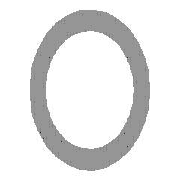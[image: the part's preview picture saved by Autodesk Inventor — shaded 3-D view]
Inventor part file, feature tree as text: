
AUTODESK INVENTOR PART (.ipt)
format: ipt  version: 2021 (Build 250183000, 183)  size: 224,768 bytes
history: native  units: mm (DEFAULTED — no unit token found)
features: other x5, plane x2, sketch x2, sweep x1
ambient origin geometry x8: Origin, YZ Plane, XZ Plane, XY Plane, X Axis, Y Axis, Z Axis, Center Point
bodies: Solid1 (feature_tree)
feature tree (10):
  parser-record x1  (decoder bookkeeping rows leaked as tree rows — omitted from the tree; the rows remain in map.json)
  other  "Driven Length"
  other  "Plano inicial"
  other  "Plano final"
  other  "Trayectoria de barrido"
  plane  "Plano de trabajo de orientación"
  sweep  "Cuerpo"
  sketch  "Sketch3"  dims[d0=26.67mm d1=2.8702mm]
  plane  "Work Plane3"
  sketch  "Sketch4"  dims[d4=-0.0mm d5=752.640106mm d6=90.0deg d7=752.640106mm d8=0.0mm d9=0.0mm]
